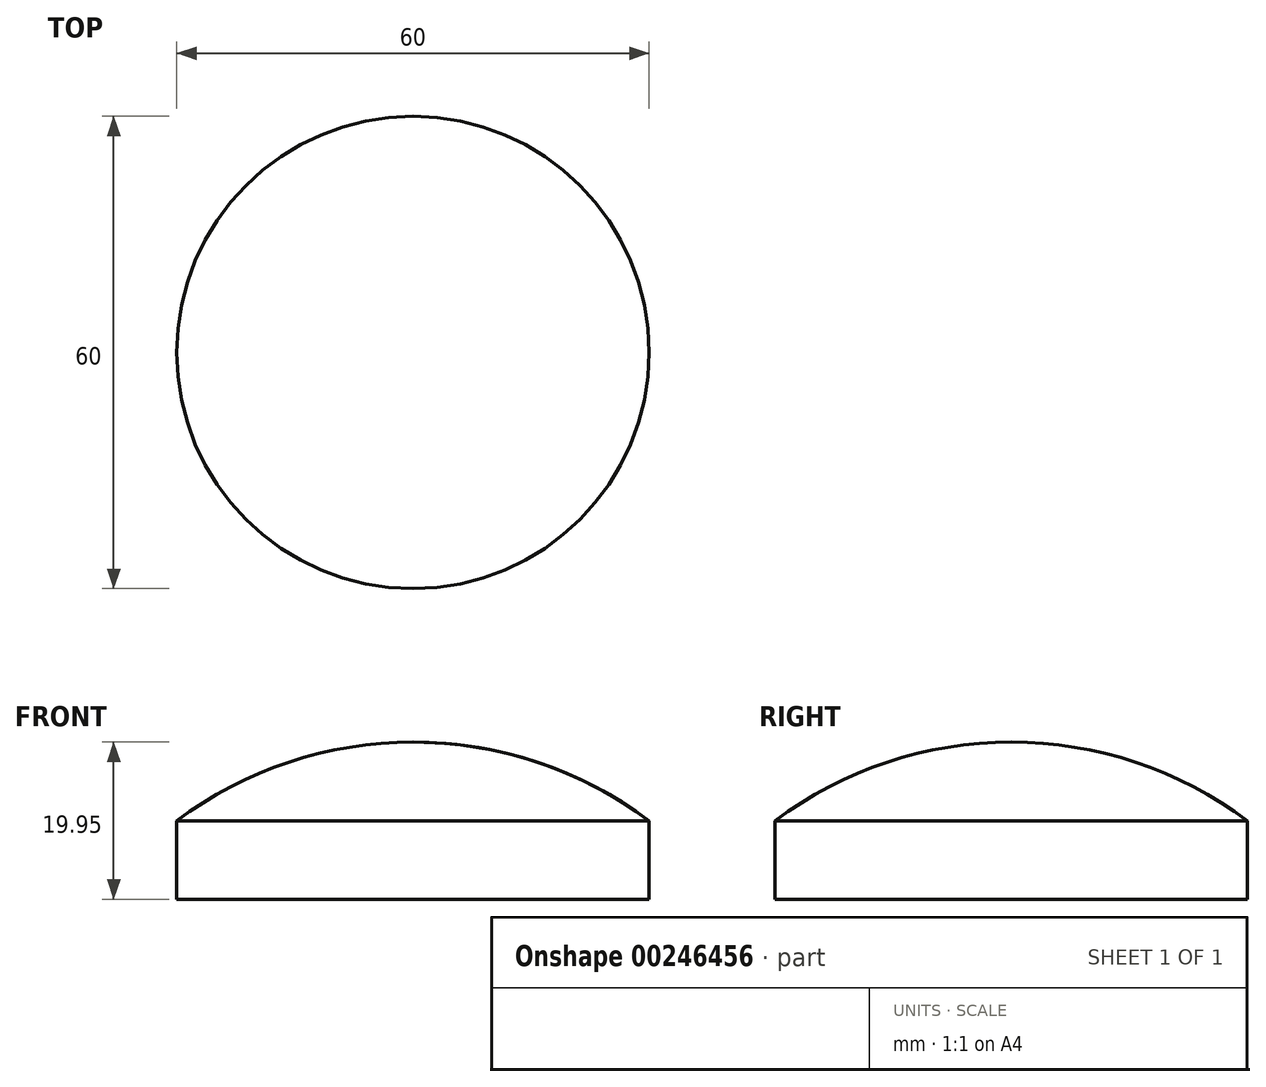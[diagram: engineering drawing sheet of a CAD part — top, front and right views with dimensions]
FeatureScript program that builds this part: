
annotation { "Feature Type Name" : "Feature", "Feature Type Description" : "" }
export const myFeature = defineFeature(function(context is Context, id is Id, definition is map)
    precondition{}
    {
        {
            var Q0;
            Q0=qCreatedBy(makeId("Front.planeOp"),FACE);
            var sketch = newSketch(context, id + "F0", { "sketchPlane" : qUnion([Q0])});
            skLineSegment(sketch, "E0", {"start": v(0, 0) * mm, "end": v(30, 0) * mm});
            skLineSegment(sketch, "E1", {"start": v(0, 0) * mm, "end": v(0, 20) * mm});
            skArc(sketch, "E2", {"start": v(30, 9.95) * mm, "mid": v(15.81, 17.39) * mm, "end": v(0, 19.95) * mm});
            skLineSegment(sketch, "E3", {"start": v(30, 0) * mm, "end": v(30, 9.95) * mm});
            skSolve(sketch);
        }
        {
            var Q0;
            Q0 = qSketchRegion(id + "F0", true);
            var Q1;
            Q1=sQuery(id+"F0.wireOp",EDGE,"E1");
            revolve(context, id + "F1", {"entities" : qUnion([Q0]), "axis" : qUnion([Q1]), "revolveType" : RevolveType.FULL});
        }
    });
